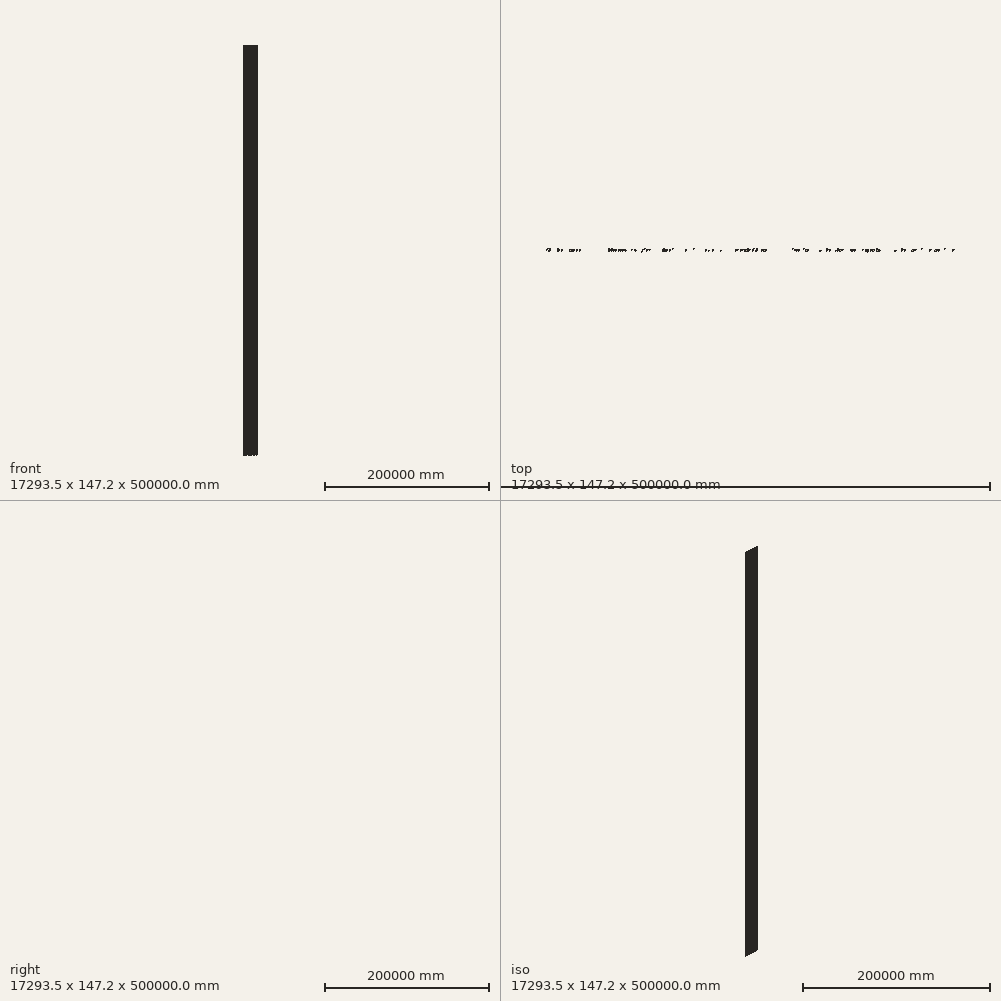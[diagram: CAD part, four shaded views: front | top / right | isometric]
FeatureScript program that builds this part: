
annotation { "Feature Type Name" : "Feature", "Feature Type Description" : "" }
export const myFeature = defineFeature(function(context is Context, id is Id, definition is map)
    precondition{}
    {
        {
            var Q0;
            Q0=qCreatedBy(makeId("Top.planeOp"),FACE);
            var sketch = newSketch(context, id + "F0", { "sketchPlane" : qUnion([Q0])});
            skText(sketch, "E0", { "text": "When, in the course of human events, it becomes necessary for one portion of the family of man to assume among the people of the earth a position different from that which they have hitherto occupied, but one to which the laws of nature and of nature", "fontName": "OpenSans-Regular.ttf"});
            const initialGuessF0  = {"E0": [-0.0623, -0.04695, 1, 0, 0.1054]};
            skSetInitialGuess(sketch, initialGuessF0);
            skSolve(sketch);
        }
        {
            var Q0;
            Q0 = qSketchRegion(id + "F0", true);
            extrude(context, id + "F1", {"entities" : qUnion([Q0]), "depth" : 500000 * mm, "offsetDistance" : 25 * mm});
        }
    });
